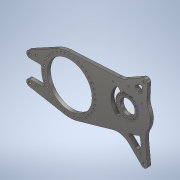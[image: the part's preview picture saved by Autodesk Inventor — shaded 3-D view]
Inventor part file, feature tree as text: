
AUTODESK INVENTOR PART (.ipt)
format: ipt  version: 2021 (Build 250183000, 183)  size: 540,160 bytes
history: native  units: in
note: dims shown in document units (in); Inventor stores cm internally (conversion verified against a paired STEP export)
features: sketch x14, extrude x11, hole x3, projected_geometry x3, chamfer x1, fillet x1
ambient origin geometry x8: Origin, YZ Plane, XZ Plane, XY Plane, X Axis, Y Axis, Z Axis, Center Point
bodies: Body1 (feature_tree)
feature tree (33):
  extrude  "Extrusion24"  Depth=2.16in
  extrude  "Extrusion28"  Depth=9.0in
  hole  "Hole9"  [1 undecoded]
  hole  "Hole11"  [1 undecoded]
  hole  "Hole13"  [1 undecoded]
  extrude  "Extrusion30"  Depth=1.5in
  extrude  "Extrusion31"  Depth=0.5in
  extrude  "Extrusion32"  Depth=0.25in
  extrude  "Extrusion33"  Depth=7.75in
  extrude  "Extrusion34"  Depth=0.25in
  chamfer  "Chamfer2"  Distance=0.0481in
  sketch  "Sketch58"  dims[d289=17.223in d290=7.75in]
  extrude  "Extrusion42"  Depth=2.75in
  extrude  "Extrusion46"  Depth=2.75in
  fillet  "Fillet6"  Radius=0.271in
  sketch  "Sketch71"  dims[d295=0.257in d296=0.75in d297=0.438in d298=0.25in d299=0.5635in d300=1.0in d301=0.8108in d302=0.1718in]
  extrude  "Extrusion50"  Depth=2.75in
  extrude  "Extrusion51"  Depth=0.5in
  sketch  "Sketch2"  dims[d9=8.5in d92=2.16in]
  sketch  "Sketch35"  dims[d118=0.75in d119=0.75in d120=0.75in d121=0.75in d137=9.0in d142=6.5in]
  projected_geometry  "Projected Loop2"
  sketch  "Sketch36"  dims[d143=1.0in d210=1.0in]
  sketch  "Sketch40"  dims[d211=6.0in d212=6.0in]
  sketch  "Sketch43"  dims[d213=3.718in d214=1.0in]
  sketch  "Sketch47"  dims[d235=10.718in d237=1.5in]
  sketch  "Sketch48"  dims[d239=0.5in d240=0.0in d266=6.75in]
  sketch  "Sketch49"  dims[d267=0.5in d268=0.0in]
  sketch  "Sketch50"  dims[d269=0.386in d270=0.75in d271=0.762in d272=0.25in d273=0.5635in d274=0.484in d275=0.8108in d288=5.0in]
  sketch  "Sketch67"  dims[d291=3.5433in d293=360.0deg]
  sketch  "Sketch72"  dims[d303=15.0deg]
  sketch  "Sketch73"  dims[d316=1.0in d317=0.0481in d318=1.0in d319=0.3972in d322=0.271in d323=0.1355in d324=0.5in d325=0.266in d326=0.75in d327=0.507in d328=0.25in d329=0.5635in d330=1.0in d331=0.8108in d347=1.0in d348=0.0in d349=0.75in d350=0.75in d351=0.5in d353=0.75in d354=0.75in d355=0.25in d356=1.0in d357=0.0in d358=0.25in d359=1.0in d360=0.0in d361=1.0in d362=1.0in d363=0.25in d364=1.0in d365=0.0in d366=2.5in d367=1.0in d368=0.0in d373=0.0156in d374=0.125in d375=45.0deg d435=1.0in d436=0.0in d456=2.25in d457=8.715in d466=3.6in d467=5.0in d468=45.0deg d469=1.5in d470=1.0in d471=0.0in d472=0.25in d502=0.315in d503=1.0in d504=0.0in d505=0.25in d506=0.25in d507=0.25in d508=1.5in d509=2.0in d510=2.75in d511=2.25in d512=2.325in d513=1.0in d514=0.0in]
  projected_geometry  "Project Cut Edges2"
  projected_geometry  "Project Cut Edges4"
note: 3 required parameter values undecoded (feature->parameter linkage not recoverable at this tier; creation-order binding heuristic only, values carry confidence <= 0.55)
